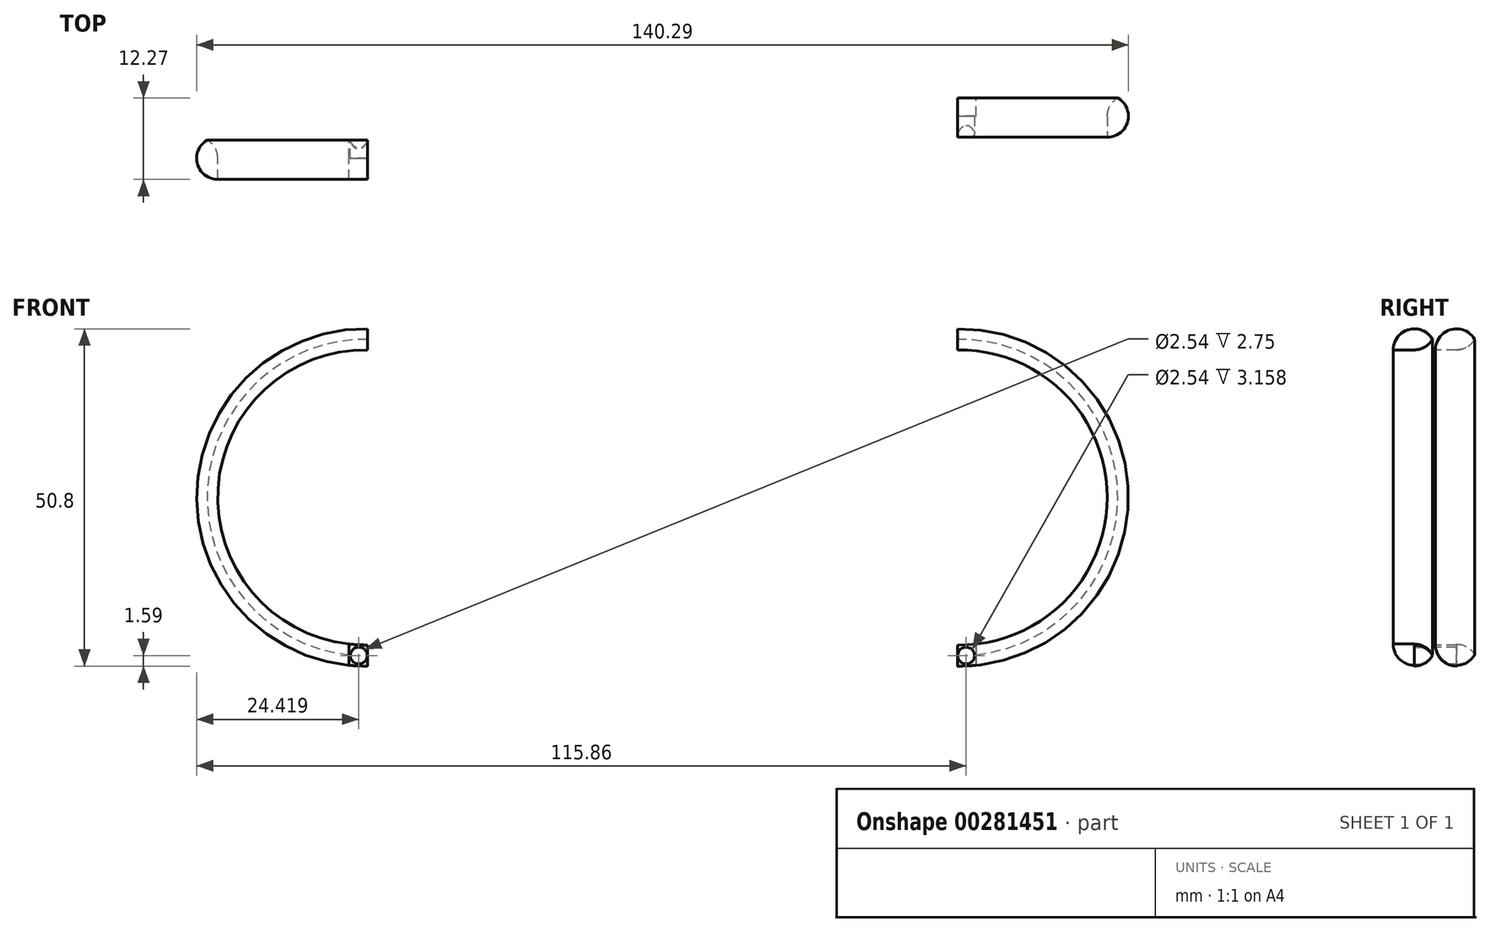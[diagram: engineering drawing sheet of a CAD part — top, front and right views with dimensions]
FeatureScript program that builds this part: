
annotation { "Feature Type Name" : "Feature", "Feature Type Description" : "" }
export const myFeature = defineFeature(function(context is Context, id is Id, definition is map)
    precondition{}
    {
        {
            var Q0;
            Q0=qCreatedBy(makeId("Front.planeOp"),FACE);
            var sketch = newSketch(context, id + "F0", { "sketchPlane" : qUnion([Q0])});
            skArc(sketch, "E0", {"start": v(20.13, -25.4) * mm, "mid": v(45.88, 0) * mm, "end": v(20.13, 25.4) * mm});
            skArc(sketch, "E1", {"start": v(-68.66, 25.4) * mm, "mid": v(-94.4, 0) * mm, "end": v(-68.66, -25.4) * mm});
            skArc(sketch, "E2", {"start": v(-68.66, 22.22) * mm, "mid": v(-91.23, 0) * mm, "end": v(-68.66, -22.22) * mm});
            skArc(sketch, "E3", {"start": v(20.13, -22.22) * mm, "mid": v(42.7, 0) * mm, "end": v(20.13, 22.22) * mm});
            skLineSegment(sketch, "E4", {"start": v(20.13, 25.4) * mm, "end": v(20.13, 22.22) * mm});
            skLineSegment(sketch, "E5.trimOffspring", {"start": v(20.13, -22.22) * mm, "end": v(20.13, -25.4) * mm});
            skLineSegment(sketch, "E6", {"start": v(-68.66, 25.4) * mm, "end": v(-68.66, 22.22) * mm});
            skLineSegment(sketch, "E7.trimOffspring", {"start": v(-68.66, -22.22) * mm, "end": v(-68.66, -25.4) * mm});
            skCircle(sketch, "E8", {"center": v(-70, -23.8) * mm, "radius": 1.27 * mm});
            skCircle(sketch, "E9", {"center": v(21.45, -23.8) * mm, "radius": 1.27 * mm});
            skPoint(sketch, "E10.start.orphan", {"position": v(20.13, -23.8) * mm});
            skPoint(sketch, "E11.start.orphan", {"position": v(-68.66, -23.8) * mm});
            skPoint(sketch, "E12", {"position": v(22.92, -25.28) * mm});
            skLineSegment(sketch, "E13", {"start": v(22.92, -25.28) * mm, "end": v(22.92, -22.09) * mm});
            skPoint(sketch, "E14", {"position": v(-71.45, -25.28) * mm});
            skLineSegment(sketch, "E15", {"start": v(-71.45, -25.28) * mm, "end": v(-71.45, -22.09) * mm});
            skSolve(sketch);
        }
        {
            var Q0;
            {var subQ0=sQuery(id+"F0.wireOp",EDGE,"E6");Q0=makeQuery(id+"F0.imprint","IMPRINT",FACE,{"disambiguationData":[TD([[makeQuery(id+"F0.imprint","IMPRINT",EDGE,{"derivedFrom":subQ0}),-1.0]])]});}
            extrude(context, id + "F1", {"entities" : qUnion([Q0]), "depth" : 6.35 * mm});
        }
        {
            var Q0;
            {var subQ0=sQuery(id+"F0.wireOp",EDGE,"E7.trimOffspring");Q0=makeQuery(id+"F0.imprint","IMPRINT",FACE,{"disambiguationData":[TD([[makeQuery(id+"F0.imprint","IMPRINT",EDGE,{"derivedFrom":subQ0}),-1.0]])]});}
            extrude(context, id + "F2", {"entities" : qUnion([Q0]), "depth" : 3.17 * mm});
        }
        {
            var Q0;
            {var subQ0=sQuery(id+"F0.wireOp",EDGE,"E5.trimOffspring");Q0=makeQuery(id+"F0.imprint","IMPRINT",FACE,{"disambiguationData":[TD([[makeQuery(id+"F0.imprint","IMPRINT",EDGE,{"derivedFrom":subQ0}),1.0]])]});}
            extrude(context, id + "F3", {"entities" : qUnion([Q0]), "oppositeDirection" : true, "depth" : 3.17 * mm});
        }
        {
            var Q0;
            {var subQ0=sQuery(id+"F0.wireOp",EDGE,"E4");Q0=makeQuery(id+"F0.imprint","IMPRINT",FACE,{"disambiguationData":[TD([[makeQuery(id+"F0.imprint","IMPRINT",EDGE,{"derivedFrom":subQ0}),1.0]])]});}
            extrude(context, id + "F4", {"entities" : qUnion([Q0]), "operationType" : NewBodyOperationType.ADD, "oppositeDirection" : true, "depth" : 6.35 * mm});
        }
        {
            var Q0;
            Q0=makeQuery(id+"F1.opExtrude","CAP_EDGE",EDGE,{"disambiguationData":[OSD([sQuery(id+"F0.wireOp",EDGE,"E1")])],"isStart":true});
            var Q1;
            Q1=makeQuery(id+"F1.opExtrude","CAP_EDGE",EDGE,{"disambiguationData":[OSD([sQuery(id+"F0.wireOp",EDGE,"E1")])],"isStart":false});
            var Q2;
            Q2=makeQuery(id+"F4.opExtrude","CAP_EDGE",EDGE,{"disambiguationData":[OSD([sQuery(id+"F0.wireOp",EDGE,"E0")])],"isStart":false});
            var Q3;
            Q3=makeQuery(id+"F4.opExtrude","CAP_EDGE",EDGE,{"disambiguationData":[OSD([sQuery(id+"F0.wireOp",EDGE,"E3")])],"isStart":false});
            var Q4;
            Q4=makeQuery(id+"F1.opExtrude","CAP_EDGE",EDGE,{"disambiguationData":[OSD([sQuery(id+"F0.wireOp",EDGE,"E2")])],"isStart":true});
            var Q5;
            {var subQ0=sQuery(id+"F0.wireOp",EDGE,"E0");Q5=makeQuery(id+"F4.boolean.opBoolean","MERGE",EDGE,{"derivedFrom":[makeQuery(id+"F3.opExtrude","CAP_EDGE",EDGE,{"disambiguationData":[OSD([subQ0])],"isStart":true}),makeQuery(id+"F4.opExtrude","CAP_EDGE",EDGE,{"disambiguationData":[OSD([subQ0])],"isStart":true})]});}
            var Q6;
            Q6=makeQuery(id+"F2.opExtrude","CAP_EDGE",EDGE,{"disambiguationData":[OSD([sQuery(id+"F0.wireOp",EDGE,"E1")])],"isStart":true});
            var Q7;
            Q7=makeQuery(id+"F2.opExtrude","CAP_EDGE",EDGE,{"disambiguationData":[OSD([sQuery(id+"F0.wireOp",EDGE,"E2")])],"isStart":true});
            fillet(context, id + "F5", {"entities" : qUnion([Q0, Q1, Q2, Q3, Q4, Q5, Q6, Q7]), "radius" : 3.17 * mm, "tangentPropagation" : true, "allowEdgeOverflow" : false});
        }
    });
